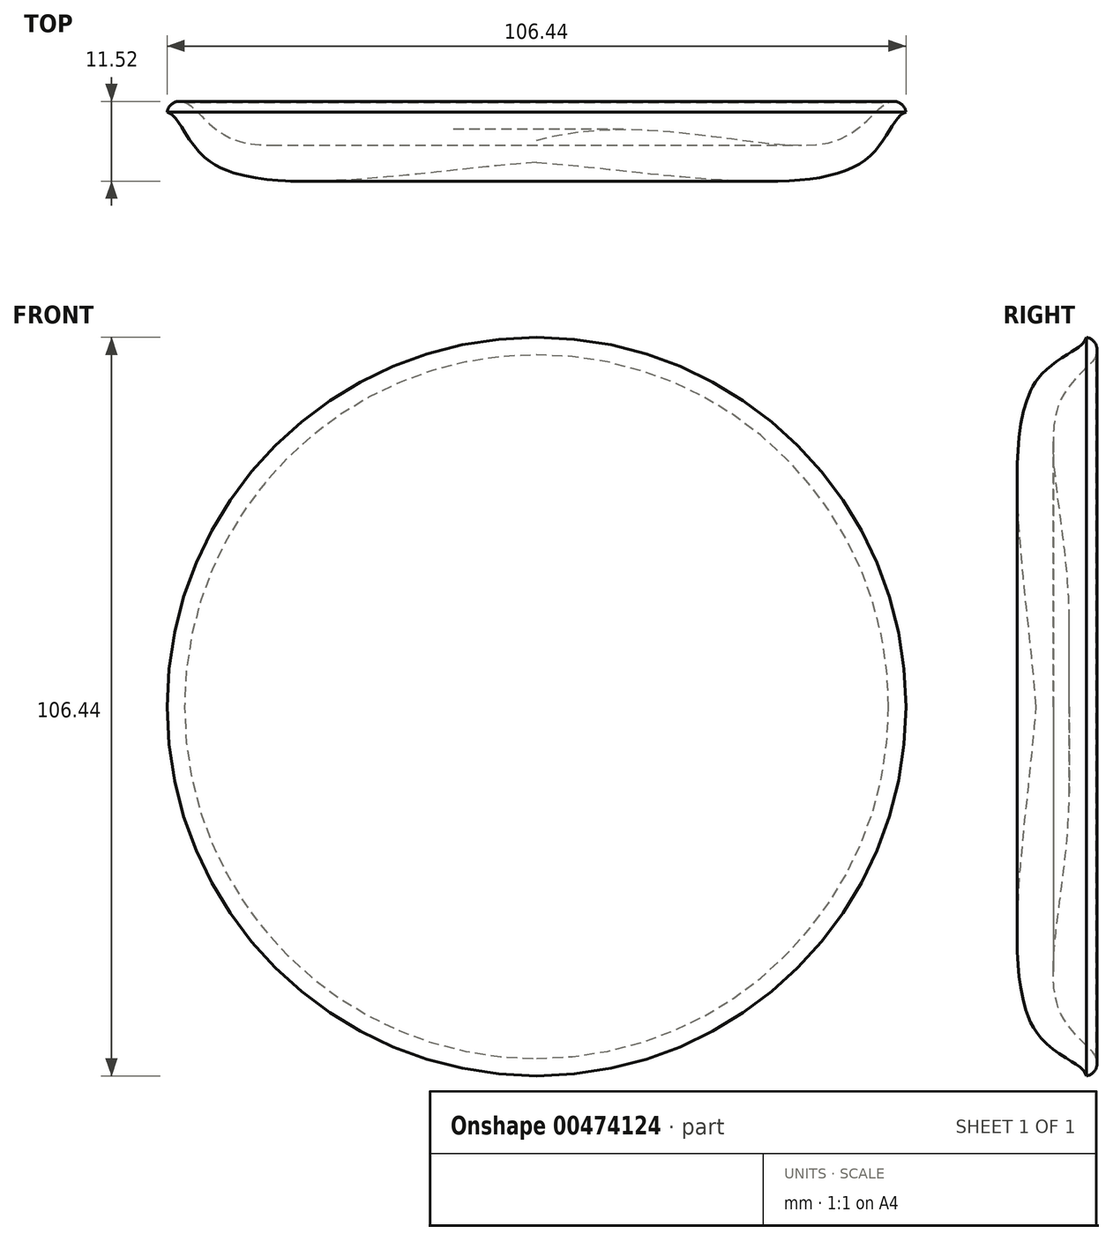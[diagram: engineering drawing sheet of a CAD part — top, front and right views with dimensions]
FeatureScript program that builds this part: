
annotation { "Feature Type Name" : "Feature", "Feature Type Description" : "" }
export const myFeature = defineFeature(function(context is Context, id is Id, definition is map)
    precondition{}
    {
        {
            var Q0;
            Q0=qCreatedBy(makeId("Top.planeOp"),FACE);
            var sketch = newSketch(context, id + "F0", { "sketchPlane" : qUnion([Q0])});
            skLineSegment(sketch, "E0", {"start": v(0, -7.9) * mm, "end": v(0, -4.72) * mm});
            skFitSpline(sketch, "E1", {"points": [v(0, -4.72) * mm, v(43.37, -4.72) * mm, v(50.71, 0.74) * mm], "startDerivative": vector(74.53, 20.67) * mm, "endDerivative": vector(14.6, 3.49) * mm});
            skArc(sketch, "E2", {"start": v(53.22, -0.66) * mm, "mid": v(52.3, 0.64) * mm, "end": v(50.71, 0.74) * mm});
            skFitSpline(sketch, "E3", {"points": [v(0, -7.9) * mm, v(46.92, -7.9) * mm, v(53.22, -0.66) * mm], "startDerivative": vector(78.78, -6.33) * mm, "endDerivative": vector(17.88, 4.21) * mm});
            skSolve(sketch);
        }
        {
            var Q0;
            Q0=makeQuery(id+"F0.imprint","IMPRINT",FACE,{"disambiguationData":[TD([[makeQuery(id+"F0.imprint","IMPRINT",EDGE,{"derivedFrom":sQuery(id+"F0.wireOp",EDGE,"E0")}),-1.0]])]});
            var Q1;
            Q1=sQuery(id+"F0.wireOp",EDGE,"E0");
            revolve(context, id + "F1", {"entities" : qUnion([Q0]), "axis" : qUnion([Q1]), "revolveType" : RevolveType.FULL});
        }
    });
